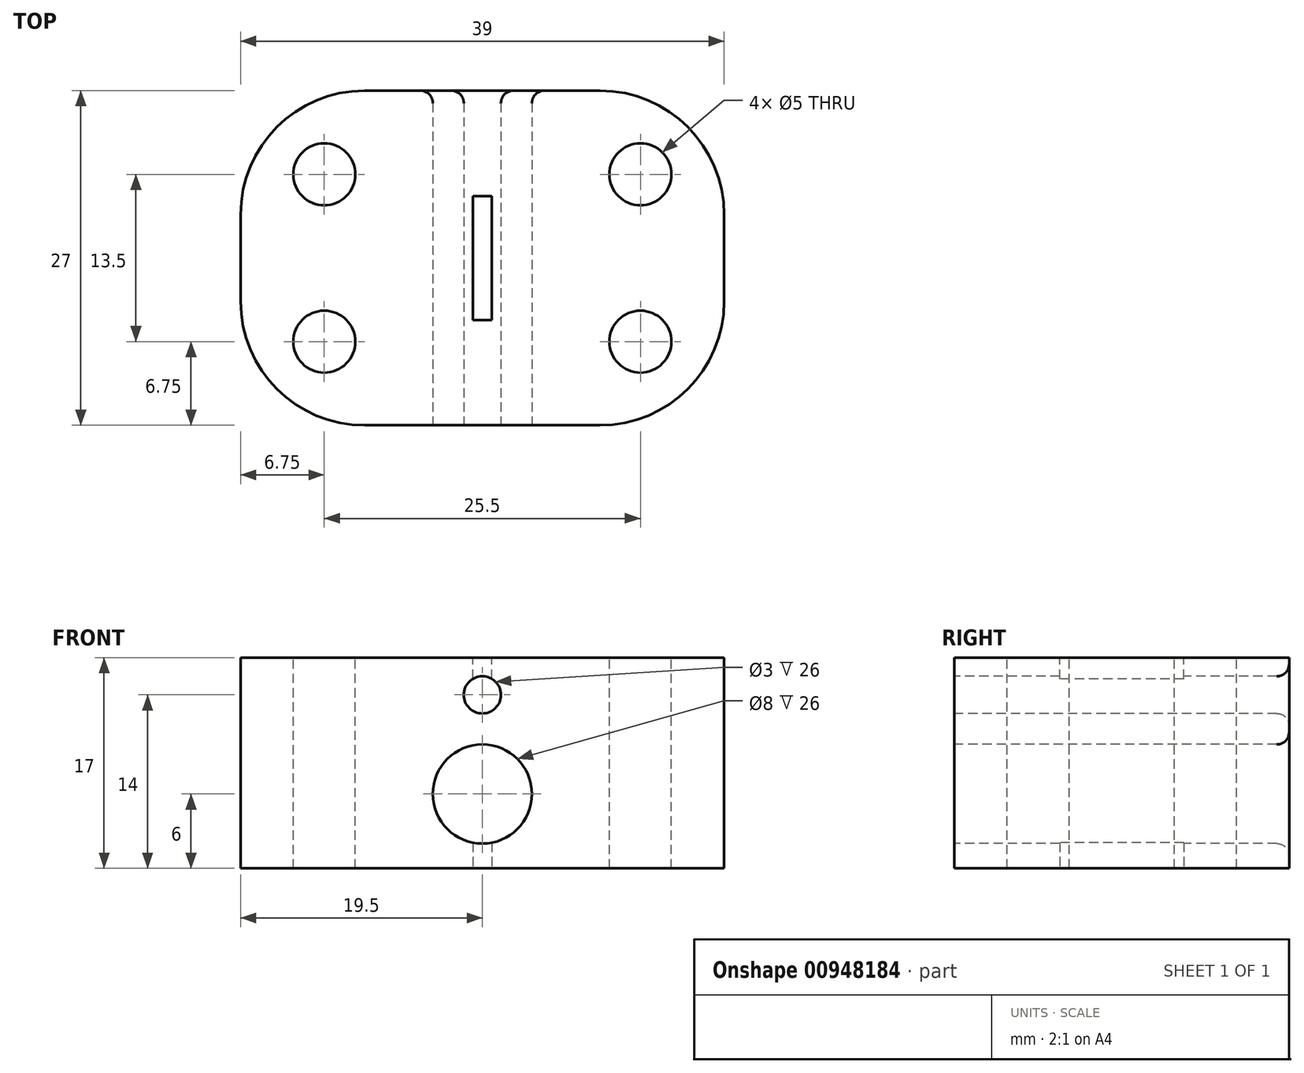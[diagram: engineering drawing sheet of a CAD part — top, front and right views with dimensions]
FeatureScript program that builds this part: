
annotation { "Feature Type Name" : "Feature", "Feature Type Description" : "" }
export const myFeature = defineFeature(function(context is Context, id is Id, definition is map)
    precondition{}
    {
        {
            var Q0;
            Q0=qCreatedBy(makeId("Top.planeOp"),FACE);
            var sketch = newSketch(context, id + "F0", { "sketchPlane" : qUnion([Q0])});
            skLineSegment(sketch, "E0.bottom", {"start": v(19.5, 13.5) * mm, "end": v(-19.5, 13.5) * mm});
            skLineSegment(sketch, "E0.top", {"start": v(19.5, -13.5) * mm, "end": v(-19.5, -13.5) * mm});
            skLineSegment(sketch, "E0.left", {"start": v(19.5, 13.5) * mm, "end": v(19.5, -13.5) * mm});
            skLineSegment(sketch, "E0.right", {"start": v(-19.5, 13.5) * mm, "end": v(-19.5, -13.5) * mm});
            skPoint(sketch, "E0.middle", {"position": v(0, 0) * mm});
            skSolve(sketch);
        }
        {
            var Q0;
            Q0=qSketchRegion(id+"F0",true);
            extrude(context, id + "F1", {"entities" : qUnion([Q0]), "depth" : 17 * mm, "offsetDistance" : 25 * mm});
        }
        {
            var Q0;
            Q0=makeQuery(id+"F1.opExtrude","SWEPT_EDGE",EDGE,{"disambiguationData":[OSD([sQuery(id+"F0.wireOp",EDGE,"E0.bottom"),sQuery(id+"F0.wireOp",EDGE,"E0.left")])]});
            var Q1;
            Q1=makeQuery(id+"F1.opExtrude","SWEPT_EDGE",EDGE,{"disambiguationData":[OSD([sQuery(id+"F0.wireOp",EDGE,"E0.bottom"),sQuery(id+"F0.wireOp",EDGE,"E0.right")])]});
            var Q2;
            Q2=makeQuery(id+"F1.opExtrude","SWEPT_EDGE",EDGE,{"disambiguationData":[OSD([sQuery(id+"F0.wireOp",EDGE,"E0.top"),sQuery(id+"F0.wireOp",EDGE,"E0.right")])]});
            var Q3;
            Q3=makeQuery(id+"F1.opExtrude","SWEPT_EDGE",EDGE,{"disambiguationData":[OSD([sQuery(id+"F0.wireOp",EDGE,"E0.top"),sQuery(id+"F0.wireOp",EDGE,"E0.left")])]});
            fillet(context, id + "F2", {"entities" : qUnion([Q0, Q1, Q2, Q3]), "radius" : 10 * mm, "tangentPropagation" : true, "defaultsChanged" : true, "vertexSettings" : [], "allowEdgeOverflow" : false});
        }
        {
            var Q0;
            Q0=makeQuery(id+"F1.opExtrude","CAP_FACE",FACE,{"disambiguationData":[OSD([sQuery(id+"F0.wireOp",EDGE,"E0.bottom"),sQuery(id+"F0.wireOp",EDGE,"E0.top"),sQuery(id+"F0.wireOp",EDGE,"E0.left"),sQuery(id+"F0.wireOp",EDGE,"E0.right")])],"isStart":false});
            var sketch = newSketch(context, id + "F3", { "sketchPlane" : qUnion([Q0])});
            skCircle(sketch, "E1", {"center": v(-12.75, -6.75) * mm, "radius": 2.5 * mm});
            skCircle(sketch, "E2", {"center": v(12.75, 6.75) * mm, "radius": 2.5 * mm});
            skCircle(sketch, "E3", {"center": v(12.75, -6.75) * mm, "radius": 2.5 * mm});
            skCircle(sketch, "E4", {"center": v(-12.75, 6.75) * mm, "radius": 2.5 * mm});
            skSolve(sketch);
        }
        {
            var Q0;
            Q0=qSketchRegion(id+"F3",true);
            extrude(context, id + "F4", {"entities" : qUnion([Q0]), "operationType" : NewBodyOperationType.REMOVE, "endBound" : BoundingType.THROUGH_ALL, "oppositeDirection" : true, "depth" : 25 * mm, "offsetDistance" : 25 * mm});
        }
        {
            var Q0;
            Q0=makeQuery(id+"F1.opExtrude","SWEPT_FACE",FACE,{"disambiguationData":[OSD([sQuery(id+"F0.wireOp",EDGE,"E0.top")])]});
            var sketch = newSketch(context, id + "F5", { "sketchPlane" : qUnion([Q0])});
            skCircle(sketch, "E5", {"center": v(0, 14) * mm, "radius": 1.5 * mm});
            skPoint(sketch, "E5.centerSnap0", {"position": v(0, 17) * mm});
            skLineSegment(sketch, "E6", {"start": v(0, 17) * mm, "end": v(2, 17) * mm, "construction": true});
            skLineSegment(sketch, "E7", {"start": v(0, 17) * mm, "end": v(-2.04, 17) * mm, "construction": true});
            skLineSegment(sketch, "E8", {"start": v(0, 17) * mm, "end": v(0, 14) * mm, "construction": true});
            skSolve(sketch);
        }
        {
            var Q0;
            Q0 = qSketchRegion(id + "F5", true);
            extrude(context, id + "F6", {"entities" : qUnion([Q0]), "operationType" : NewBodyOperationType.REMOVE, "endBound" : BoundingType.THROUGH_ALL, "oppositeDirection" : true, "depth" : 25 * mm, "offsetDistance" : 25 * mm});
        }
        {
            var Q0;
            Q0=makeQuery(id+"F1.opExtrude","CAP_FACE",FACE,{"disambiguationData":[OSD([sQuery(id+"F0.wireOp",EDGE,"E0.bottom"),sQuery(id+"F0.wireOp",EDGE,"E0.top"),sQuery(id+"F0.wireOp",EDGE,"E0.left"),sQuery(id+"F0.wireOp",EDGE,"E0.right")])],"isStart":false});
            var sketch = newSketch(context, id + "F7", { "sketchPlane" : qUnion([Q0])});
            skLineSegment(sketch, "E9", {"start": v(0, 13.5) * mm, "end": v(0, -13.5) * mm, "construction": true});
            skLineSegment(sketch, "E10", {"start": v(19.5, 0) * mm, "end": v(0, 0) * mm, "construction": true});
            skLineSegment(sketch, "E11.bottom", {"start": v(0.75, -5) * mm, "end": v(-0.75, -5) * mm});
            skLineSegment(sketch, "E11.top", {"start": v(0.75, 5) * mm, "end": v(-0.75, 5) * mm});
            skLineSegment(sketch, "E11.left", {"start": v(0.75, -5) * mm, "end": v(0.75, 5) * mm});
            skLineSegment(sketch, "E11.right", {"start": v(-0.75, -5) * mm, "end": v(-0.75, 5) * mm});
            skPoint(sketch, "E11.middle", {"position": v(0, 0) * mm});
            skSolve(sketch);
        }
        {
            var Q0;
            Q0 = qSketchRegion(id + "F7", true);
            extrude(context, id + "F8", {"entities" : qUnion([Q0]), "operationType" : NewBodyOperationType.REMOVE, "endBound" : BoundingType.UP_TO_NEXT, "oppositeDirection" : true, "depth" : 3 * mm, "offsetDistance" : 25 * mm});
        }
        {
            var Q0;
            Q0=makeQuery(id+"F1.opExtrude","SWEPT_FACE",FACE,{"disambiguationData":[OSD([sQuery(id+"F0.wireOp",EDGE,"E0.top")])]});
            var sketch = newSketch(context, id + "F9", { "sketchPlane" : qUnion([Q0])});
            skCircle(sketch, "E12", {"center": v(0, 6) * mm, "radius": 4 * mm});
            skPoint(sketch, "E12.centerSnap0", {"position": v(0, 0) * mm});
            skSolve(sketch);
        }
        {
            var Q0;
            Q0 = qSketchRegion(id + "F9", true);
            extrude(context, id + "F10", {"entities" : qUnion([Q0]), "operationType" : NewBodyOperationType.REMOVE, "endBound" : BoundingType.THROUGH_ALL, "oppositeDirection" : true, "depth" : 25 * mm, "offsetDistance" : 25 * mm});
        }
        {
            var Q0;
            Q0=makeQuery(id+"F6.boolean.opBoolean","COPY",EDGE,{"derivedFrom":makeQuery(id+"F6.opExtrude","CAP_EDGE",EDGE,{"disambiguationData":[OSD([sQuery(id+"F5.wireOp",EDGE,"E5")])],"isStart":true})});
            var Q1;
            Q1=makeQuery(id+"F6.boolean.opBoolean","INTERSECT",EDGE,{"derivedFrom":[makeQuery(id+"F1.opExtrude","SWEPT_FACE",FACE,{"disambiguationData":[OSD([sQuery(id+"F0.wireOp",EDGE,"E0.bottom")])]}),makeQuery(id+"F6.opExtrude","SWEPT_FACE",FACE,{"disambiguationData":[OSD([sQuery(id+"F5.wireOp",EDGE,"E5")])]})]});
            var Q2;
            Q2=makeQuery(id+"F10.boolean.opBoolean","COPY",EDGE,{"derivedFrom":makeQuery(id+"F10.opExtrude","CAP_EDGE",EDGE,{"disambiguationData":[OSD([sQuery(id+"F9.wireOp",EDGE,"E12")])],"isStart":true})});
            var Q3;
            Q3=makeQuery(id+"F10.boolean.opBoolean","INTERSECT",EDGE,{"derivedFrom":[makeQuery(id+"F1.opExtrude","SWEPT_FACE",FACE,{"disambiguationData":[OSD([sQuery(id+"F0.wireOp",EDGE,"E0.bottom")])]}),makeQuery(id+"F10.opExtrude","SWEPT_FACE",FACE,{"disambiguationData":[OSD([sQuery(id+"F9.wireOp",EDGE,"E12")])]})]});
            fillet(context, id + "F11", {"entities" : qUnion([Q0, Q1, Q2, Q3]), "radius" : 1 * mm, "tangentPropagation" : true, "allowEdgeOverflow" : false});
        }
        {
            var Q0;
            Q0=makeQuery(id+"F1.opExtrude","CAP_FACE",FACE,{"disambiguationData":[OSD([sQuery(id+"F0.wireOp",EDGE,"E0.bottom"),sQuery(id+"F0.wireOp",EDGE,"E0.top"),sQuery(id+"F0.wireOp",EDGE,"E0.left"),sQuery(id+"F0.wireOp",EDGE,"E0.right")])],"isStart":true});
            var sketch = newSketch(context, id + "F12", { "sketchPlane" : qUnion([Q0])});
            skLineSegment(sketch, "E13.bottom", {"start": v(0.75, -5) * mm, "end": v(-0.75, -5) * mm});
            skLineSegment(sketch, "E13.top", {"start": v(0.75, 5) * mm, "end": v(-0.75, 5) * mm});
            skLineSegment(sketch, "E13.left", {"start": v(0.75, -5) * mm, "end": v(0.75, 5) * mm});
            skLineSegment(sketch, "E13.right", {"start": v(-0.75, -5) * mm, "end": v(-0.75, 5) * mm});
            skPoint(sketch, "E13.middle", {"position": v(0, 0) * mm});
            skPoint(sketch, "E13.middle.positionSnap0", {"position": v(19.5, 0) * mm});
            skPoint(sketch, "E13.middle.positionSnap1", {"position": v(0, 13.5) * mm});
            skPoint(sketch, "E13.centerSnap0", {"position": v(19.5, 0) * mm});
            skPoint(sketch, "E13.centerSnap1", {"position": v(0, 13.5) * mm});
            skSolve(sketch);
        }
        {
            var Q0;
            Q0 = qSketchRegion(id + "F12", true);
            extrude(context, id + "F13", {"entities" : qUnion([Q0]), "operationType" : NewBodyOperationType.REMOVE, "endBound" : BoundingType.UP_TO_NEXT, "oppositeDirection" : true, "depth" : 25 * mm, "offsetDistance" : 25 * mm});
        }
    });
